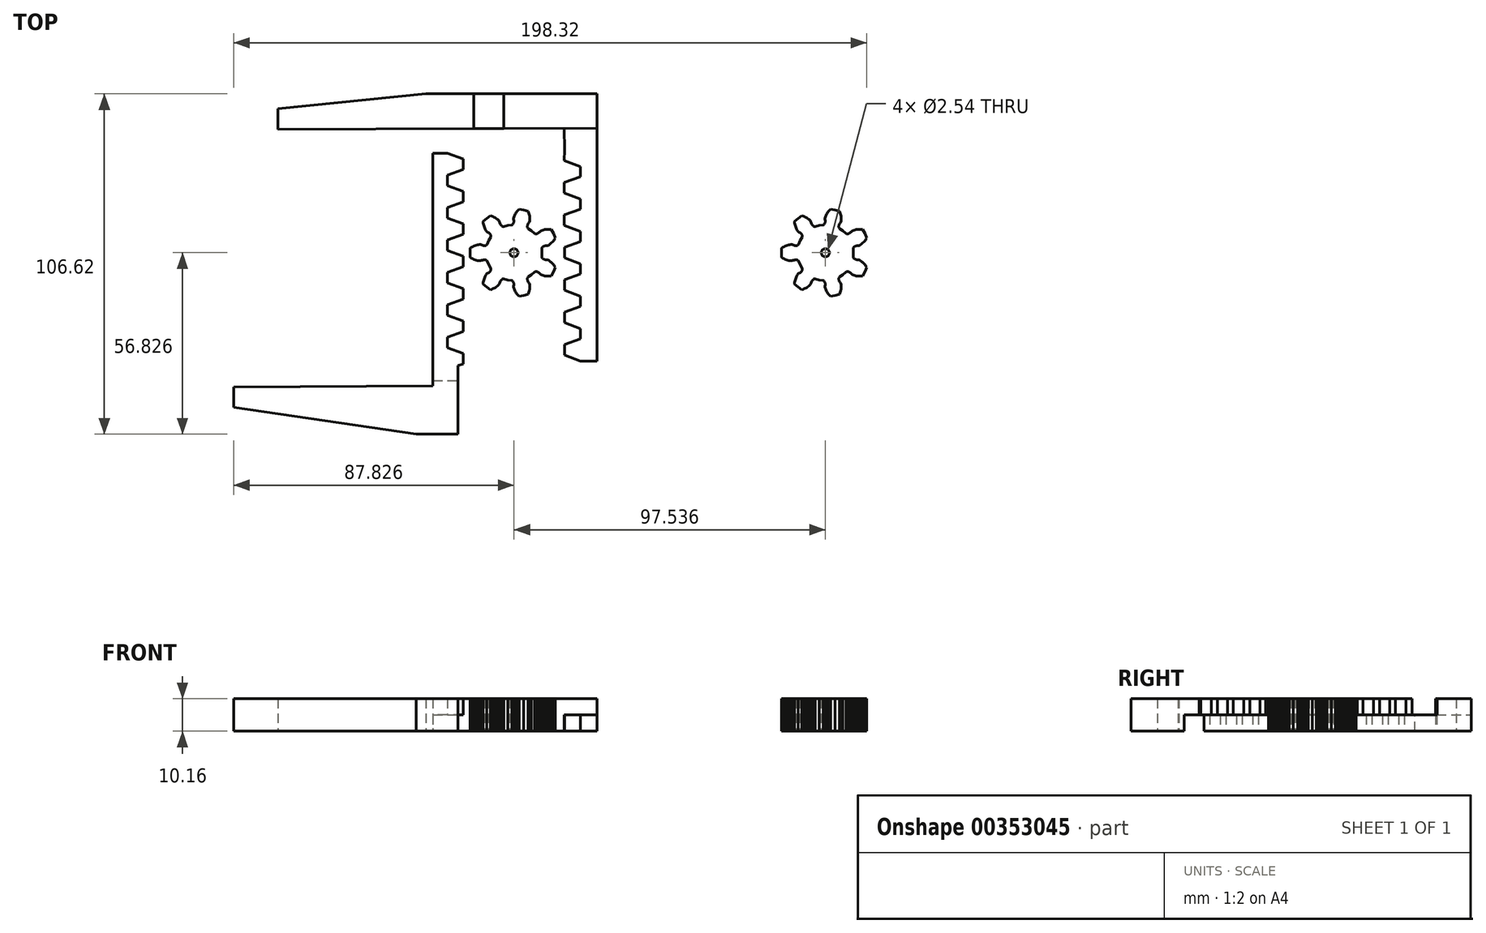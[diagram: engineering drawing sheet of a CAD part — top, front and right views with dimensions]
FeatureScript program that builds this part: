
annotation { "Feature Type Name" : "Feature", "Feature Type Description" : "" }
export const myFeature = defineFeature(function(context is Context, id is Id, definition is map)
    precondition{}
    {
        {
            var Q0;
            Q0=qCreatedBy(makeId("Top.planeOp"),FACE);
            var sketch = newSketch(context, id + "F0", { "sketchPlane" : qUnion([Q0])});
            skLineSegment(sketch, "E0", {"start": v(32.97, 4.76) * mm, "end": v(33, 5.04) * mm});
            skLineSegment(sketch, "E1", {"start": v(33, 5.04) * mm, "end": v(33.07, 5.15) * mm});
            skLineSegment(sketch, "E2", {"start": v(33.07, 5.15) * mm, "end": v(33.14, 5.24) * mm});
            skLineSegment(sketch, "E3", {"start": v(33.14, 5.24) * mm, "end": v(33.2, 5.3) * mm});
            skLineSegment(sketch, "E4", {"start": v(33.2, 5.3) * mm, "end": v(33.28, 5.37) * mm});
            skLineSegment(sketch, "E5", {"start": v(33.28, 5.37) * mm, "end": v(33.36, 5.42) * mm});
            skLineSegment(sketch, "E6", {"start": v(33.36, 5.42) * mm, "end": v(33.5, 5.5) * mm});
            skLineSegment(sketch, "E7", {"start": v(33.5, 5.5) * mm, "end": v(33.66, 5.58) * mm});
            skLineSegment(sketch, "E8", {"start": v(33.66, 5.58) * mm, "end": v(33.82, 5.63) * mm});
            skLineSegment(sketch, "E9", {"start": v(33.82, 5.63) * mm, "end": v(34.14, 5.7) * mm});
            skLineSegment(sketch, "E10", {"start": v(34.14, 5.7) * mm, "end": v(34.47, 5.75) * mm});
            skLineSegment(sketch, "E11", {"start": v(34.47, 5.75) * mm, "end": v(34.8, 5.77) * mm});
            skLineSegment(sketch, "E12", {"start": v(34.8, 5.77) * mm, "end": v(35.12, 5.92) * mm});
            skLineSegment(sketch, "E13", {"start": v(35.12, 5.92) * mm, "end": v(35.41, 6.1) * mm});
            skLineSegment(sketch, "E14", {"start": v(35.41, 6.1) * mm, "end": v(35.7, 6.32) * mm});
            skLineSegment(sketch, "E15", {"start": v(35.7, 6.32) * mm, "end": v(35.98, 6.56) * mm});
            skLineSegment(sketch, "E16", {"start": v(35.98, 6.56) * mm, "end": v(36.25, 6.83) * mm});
            skLineSegment(sketch, "E17", {"start": v(36.25, 6.83) * mm, "end": v(36.52, 7.13) * mm});
            skLineSegment(sketch, "E18", {"start": v(36.52, 7.13) * mm, "end": v(36.77, 7.44) * mm});
            skLineSegment(sketch, "E19", {"start": v(36.77, 7.44) * mm, "end": v(37, 7.78) * mm});
            skLineSegment(sketch, "E20", {"start": v(37, 7.78) * mm, "end": v(37.23, 8.14) * mm});
            skLineSegment(sketch, "E21", {"start": v(37.23, 8.14) * mm, "end": v(36.67, 9.48) * mm});
            skLineSegment(sketch, "E22", {"start": v(36.67, 9.48) * mm, "end": v(35.97, 10.76) * mm});
            skLineSegment(sketch, "E23", {"start": v(35.97, 10.76) * mm, "end": v(35.55, 10.8) * mm});
            skLineSegment(sketch, "E24", {"start": v(35.55, 10.8) * mm, "end": v(35.13, 10.83) * mm});
            skLineSegment(sketch, "E25", {"start": v(35.13, 10.83) * mm, "end": v(34.73, 10.83) * mm});
            skLineSegment(sketch, "E26", {"start": v(34.73, 10.83) * mm, "end": v(34.34, 10.81) * mm});
            skLineSegment(sketch, "E27", {"start": v(34.34, 10.81) * mm, "end": v(33.96, 10.77) * mm});
            skLineSegment(sketch, "E28", {"start": v(33.96, 10.77) * mm, "end": v(33.6, 10.7) * mm});
            skLineSegment(sketch, "E29", {"start": v(33.6, 10.7) * mm, "end": v(33.24, 10.61) * mm});
            skLineSegment(sketch, "E30", {"start": v(33.24, 10.61) * mm, "end": v(32.91, 10.5) * mm});
            skLineSegment(sketch, "E31", {"start": v(32.91, 10.5) * mm, "end": v(32.6, 10.34) * mm});
            skLineSegment(sketch, "E32", {"start": v(32.6, 10.34) * mm, "end": v(32.38, 10.1) * mm});
            skLineSegment(sketch, "E33", {"start": v(32.38, 10.1) * mm, "end": v(32.14, 9.86) * mm});
            skLineSegment(sketch, "E34", {"start": v(32.14, 9.86) * mm, "end": v(31.88, 9.66) * mm});
            skLineSegment(sketch, "E35", {"start": v(31.88, 9.66) * mm, "end": v(31.74, 9.57) * mm});
            skLineSegment(sketch, "E36", {"start": v(31.74, 9.57) * mm, "end": v(31.59, 9.49) * mm});
            skLineSegment(sketch, "E37", {"start": v(31.59, 9.49) * mm, "end": v(31.43, 9.43) * mm});
            skLineSegment(sketch, "E38", {"start": v(31.43, 9.43) * mm, "end": v(31.34, 9.4) * mm});
            skLineSegment(sketch, "E39", {"start": v(31.34, 9.4) * mm, "end": v(31.25, 9.38) * mm});
            skLineSegment(sketch, "E40", {"start": v(31.25, 9.38) * mm, "end": v(31.15, 9.37) * mm});
            skLineSegment(sketch, "E41", {"start": v(31.15, 9.37) * mm, "end": v(31.04, 9.37) * mm});
            skLineSegment(sketch, "E42", {"start": v(31.04, 9.37) * mm, "end": v(30.91, 9.4) * mm});
            skLineSegment(sketch, "E43", {"start": v(30.91, 9.4) * mm, "end": v(30.67, 9.53) * mm});
            skLineSegment(sketch, "E44", {"start": v(30.67, 9.53) * mm, "end": v(29.75, 10.38) * mm});
            skLineSegment(sketch, "E45", {"start": v(29.75, 10.38) * mm, "end": v(28.72, 11.09) * mm});
            skLineSegment(sketch, "E46", {"start": v(28.72, 11.09) * mm, "end": v(28.53, 11.3) * mm});
            skLineSegment(sketch, "E47", {"start": v(28.53, 11.3) * mm, "end": v(28.48, 11.41) * mm});
            skLineSegment(sketch, "E48", {"start": v(28.48, 11.41) * mm, "end": v(28.45, 11.52) * mm});
            skLineSegment(sketch, "E49", {"start": v(28.45, 11.52) * mm, "end": v(28.44, 11.62) * mm});
            skLineSegment(sketch, "E50", {"start": v(28.44, 11.62) * mm, "end": v(28.44, 11.71) * mm});
            skLineSegment(sketch, "E51", {"start": v(28.44, 11.71) * mm, "end": v(28.45, 11.8) * mm});
            skLineSegment(sketch, "E52", {"start": v(28.45, 11.8) * mm, "end": v(28.47, 11.97) * mm});
            skLineSegment(sketch, "E53", {"start": v(28.47, 11.97) * mm, "end": v(28.52, 12.14) * mm});
            skLineSegment(sketch, "E54", {"start": v(28.52, 12.14) * mm, "end": v(28.57, 12.3) * mm});
            skLineSegment(sketch, "E55", {"start": v(28.57, 12.3) * mm, "end": v(28.71, 12.6) * mm});
            skLineSegment(sketch, "E56", {"start": v(28.71, 12.6) * mm, "end": v(28.89, 12.88) * mm});
            skLineSegment(sketch, "E57", {"start": v(28.89, 12.88) * mm, "end": v(29.08, 13.15) * mm});
            skLineSegment(sketch, "E58", {"start": v(29.08, 13.15) * mm, "end": v(29.16, 13.49) * mm});
            skLineSegment(sketch, "E59", {"start": v(29.16, 13.49) * mm, "end": v(29.2, 13.84) * mm});
            skLineSegment(sketch, "E60", {"start": v(29.2, 13.84) * mm, "end": v(29.2, 14.2) * mm});
            skLineSegment(sketch, "E61", {"start": v(29.2, 14.2) * mm, "end": v(29.2, 14.57) * mm});
            skLineSegment(sketch, "E62", {"start": v(29.2, 14.57) * mm, "end": v(29.15, 14.95) * mm});
            skLineSegment(sketch, "E63", {"start": v(29.15, 14.95) * mm, "end": v(29.08, 15.34) * mm});
            skLineSegment(sketch, "E64", {"start": v(29.08, 15.34) * mm, "end": v(29, 15.73) * mm});
            skLineSegment(sketch, "E65", {"start": v(29, 15.73) * mm, "end": v(28.88, 16.13) * mm});
            skLineSegment(sketch, "E66", {"start": v(28.88, 16.13) * mm, "end": v(28.74, 16.53) * mm});
            skLineSegment(sketch, "E67", {"start": v(28.74, 16.53) * mm, "end": v(27.34, 16.93) * mm});
            skLineSegment(sketch, "E68", {"start": v(27.34, 16.93) * mm, "end": v(25.9, 17.18) * mm});
            skLineSegment(sketch, "E69", {"start": v(25.9, 17.18) * mm, "end": v(25.6, 16.87) * mm});
            skLineSegment(sketch, "E70", {"start": v(25.6, 16.87) * mm, "end": v(25.33, 16.57) * mm});
            skLineSegment(sketch, "E71", {"start": v(25.33, 16.57) * mm, "end": v(25.07, 16.25) * mm});
            skLineSegment(sketch, "E72", {"start": v(25.07, 16.25) * mm, "end": v(24.85, 15.93) * mm});
            skLineSegment(sketch, "E73", {"start": v(24.85, 15.93) * mm, "end": v(24.64, 15.6) * mm});
            skLineSegment(sketch, "E74", {"start": v(24.64, 15.6) * mm, "end": v(24.47, 15.28) * mm});
            skLineSegment(sketch, "E75", {"start": v(24.47, 15.28) * mm, "end": v(24.32, 14.95) * mm});
            skLineSegment(sketch, "E76", {"start": v(24.32, 14.95) * mm, "end": v(24.2, 14.62) * mm});
            skLineSegment(sketch, "E77", {"start": v(24.2, 14.62) * mm, "end": v(24.13, 14.28) * mm});
            skLineSegment(sketch, "E78", {"start": v(24.13, 14.28) * mm, "end": v(24.18, 13.95) * mm});
            skLineSegment(sketch, "E79", {"start": v(24.18, 13.95) * mm, "end": v(24.22, 13.62) * mm});
            skLineSegment(sketch, "E80", {"start": v(24.22, 13.62) * mm, "end": v(24.22, 13.3) * mm});
            skLineSegment(sketch, "E81", {"start": v(24.22, 13.3) * mm, "end": v(24.2, 13.12) * mm});
            skLineSegment(sketch, "E82", {"start": v(24.2, 13.12) * mm, "end": v(24.17, 12.96) * mm});
            skLineSegment(sketch, "E83", {"start": v(24.17, 12.96) * mm, "end": v(24.11, 12.8) * mm});
            skLineSegment(sketch, "E84", {"start": v(24.11, 12.8) * mm, "end": v(24.08, 12.7) * mm});
            skLineSegment(sketch, "E85", {"start": v(24.08, 12.7) * mm, "end": v(24.04, 12.62) * mm});
            skLineSegment(sketch, "E86", {"start": v(24.04, 12.62) * mm, "end": v(23.98, 12.54) * mm});
            skLineSegment(sketch, "E87", {"start": v(23.98, 12.54) * mm, "end": v(23.92, 12.45) * mm});
            skLineSegment(sketch, "E88", {"start": v(23.92, 12.45) * mm, "end": v(23.82, 12.37) * mm});
            skLineSegment(sketch, "E89", {"start": v(23.82, 12.37) * mm, "end": v(23.56, 12.27) * mm});
            skLineSegment(sketch, "E90", {"start": v(23.56, 12.27) * mm, "end": v(22.32, 12.07) * mm});
            skLineSegment(sketch, "E91", {"start": v(22.32, 12.07) * mm, "end": v(21.13, 11.7) * mm});
            skLineSegment(sketch, "E92", {"start": v(21.13, 11.7) * mm, "end": v(20.85, 11.69) * mm});
            skLineSegment(sketch, "E93", {"start": v(20.85, 11.69) * mm, "end": v(20.72, 11.72) * mm});
            skLineSegment(sketch, "E94", {"start": v(20.72, 11.72) * mm, "end": v(20.62, 11.77) * mm});
            skLineSegment(sketch, "E95", {"start": v(20.62, 11.77) * mm, "end": v(20.54, 11.83) * mm});
            skLineSegment(sketch, "E96", {"start": v(20.54, 11.83) * mm, "end": v(20.47, 11.88) * mm});
            skLineSegment(sketch, "E97", {"start": v(20.47, 11.88) * mm, "end": v(20.4, 11.94) * mm});
            skLineSegment(sketch, "E98", {"start": v(20.4, 11.94) * mm, "end": v(20.28, 12.07) * mm});
            skLineSegment(sketch, "E99", {"start": v(20.28, 12.07) * mm, "end": v(20.18, 12.2) * mm});
            skLineSegment(sketch, "E100", {"start": v(20.18, 12.2) * mm, "end": v(20.09, 12.35) * mm});
            skLineSegment(sketch, "E101", {"start": v(20.09, 12.35) * mm, "end": v(19.94, 12.65) * mm});
            skLineSegment(sketch, "E102", {"start": v(19.94, 12.65) * mm, "end": v(19.83, 12.96) * mm});
            skLineSegment(sketch, "E103", {"start": v(19.83, 12.96) * mm, "end": v(19.74, 13.28) * mm});
            skLineSegment(sketch, "E104", {"start": v(19.74, 13.28) * mm, "end": v(19.52, 13.55) * mm});
            skLineSegment(sketch, "E105", {"start": v(19.52, 13.55) * mm, "end": v(19.28, 13.8) * mm});
            skLineSegment(sketch, "E106", {"start": v(19.28, 13.8) * mm, "end": v(19, 14.03) * mm});
            skLineSegment(sketch, "E107", {"start": v(19, 14.03) * mm, "end": v(18.7, 14.25) * mm});
            skLineSegment(sketch, "E108", {"start": v(18.7, 14.25) * mm, "end": v(18.38, 14.46) * mm});
            skLineSegment(sketch, "E109", {"start": v(18.38, 14.46) * mm, "end": v(18.03, 14.64) * mm});
            skLineSegment(sketch, "E110", {"start": v(18.03, 14.64) * mm, "end": v(17.67, 14.82) * mm});
            skLineSegment(sketch, "E111", {"start": v(17.67, 14.82) * mm, "end": v(17.29, 14.98) * mm});
            skLineSegment(sketch, "E112", {"start": v(17.29, 14.98) * mm, "end": v(16.89, 15.12) * mm});
            skLineSegment(sketch, "E113", {"start": v(16.89, 15.12) * mm, "end": v(15.7, 14.27) * mm});
            skLineSegment(sketch, "E114", {"start": v(15.7, 14.27) * mm, "end": v(14.6, 13.3) * mm});
            skLineSegment(sketch, "E115", {"start": v(14.6, 13.3) * mm, "end": v(14.66, 12.88) * mm});
            skLineSegment(sketch, "E116", {"start": v(14.66, 12.88) * mm, "end": v(14.73, 12.47) * mm});
            skLineSegment(sketch, "E117", {"start": v(14.73, 12.47) * mm, "end": v(14.82, 12.08) * mm});
            skLineSegment(sketch, "E118", {"start": v(14.82, 12.08) * mm, "end": v(14.92, 11.7) * mm});
            skLineSegment(sketch, "E119", {"start": v(14.92, 11.7) * mm, "end": v(15.05, 11.34) * mm});
            skLineSegment(sketch, "E120", {"start": v(15.05, 11.34) * mm, "end": v(15.2, 11) * mm});
            skLineSegment(sketch, "E121", {"start": v(15.2, 11) * mm, "end": v(15.36, 10.68) * mm});
            skLineSegment(sketch, "E122", {"start": v(15.36, 10.68) * mm, "end": v(15.55, 10.38) * mm});
            skLineSegment(sketch, "E123", {"start": v(15.55, 10.38) * mm, "end": v(15.77, 10.12) * mm});
            skLineSegment(sketch, "E124", {"start": v(15.77, 10.12) * mm, "end": v(16.06, 9.95) * mm});
            skLineSegment(sketch, "E125", {"start": v(16.06, 9.95) * mm, "end": v(16.34, 9.77) * mm});
            skLineSegment(sketch, "E126", {"start": v(16.34, 9.77) * mm, "end": v(16.6, 9.56) * mm});
            skLineSegment(sketch, "E127", {"start": v(16.6, 9.56) * mm, "end": v(16.72, 9.45) * mm});
            skLineSegment(sketch, "E128", {"start": v(16.72, 9.45) * mm, "end": v(16.83, 9.32) * mm});
            skLineSegment(sketch, "E129", {"start": v(16.83, 9.32) * mm, "end": v(16.92, 9.17) * mm});
            skLineSegment(sketch, "E130", {"start": v(16.92, 9.17) * mm, "end": v(16.97, 9.1) * mm});
            skLineSegment(sketch, "E131", {"start": v(16.97, 9.1) * mm, "end": v(17, 9) * mm});
            skLineSegment(sketch, "E132", {"start": v(17, 9) * mm, "end": v(17.04, 8.91) * mm});
            skLineSegment(sketch, "E133", {"start": v(17.04, 8.91) * mm, "end": v(17.06, 8.8) * mm});
            skLineSegment(sketch, "E134", {"start": v(17.06, 8.8) * mm, "end": v(17.07, 8.68) * mm});
            skLineSegment(sketch, "E135", {"start": v(17.07, 8.68) * mm, "end": v(16.99, 8.41) * mm});
            skLineSegment(sketch, "E136", {"start": v(16.99, 8.41) * mm, "end": v(16.37, 7.32) * mm});
            skLineSegment(sketch, "E137", {"start": v(16.37, 7.32) * mm, "end": v(15.9, 6.16) * mm});
            skLineSegment(sketch, "E138", {"start": v(15.9, 6.16) * mm, "end": v(15.75, 5.93) * mm});
            skLineSegment(sketch, "E139", {"start": v(15.75, 5.93) * mm, "end": v(15.64, 5.86) * mm});
            skLineSegment(sketch, "E140", {"start": v(15.64, 5.86) * mm, "end": v(15.54, 5.8) * mm});
            skLineSegment(sketch, "E141", {"start": v(15.54, 5.8) * mm, "end": v(15.45, 5.78) * mm});
            skLineSegment(sketch, "E142", {"start": v(15.45, 5.78) * mm, "end": v(15.36, 5.75) * mm});
            skLineSegment(sketch, "E143", {"start": v(15.36, 5.75) * mm, "end": v(15.27, 5.74) * mm});
            skLineSegment(sketch, "E144", {"start": v(15.27, 5.74) * mm, "end": v(15.1, 5.72) * mm});
            skLineSegment(sketch, "E145", {"start": v(15.1, 5.72) * mm, "end": v(14.93, 5.73) * mm});
            skLineSegment(sketch, "E146", {"start": v(14.93, 5.73) * mm, "end": v(14.76, 5.75) * mm});
            skLineSegment(sketch, "E147", {"start": v(14.76, 5.75) * mm, "end": v(14.44, 5.82) * mm});
            skLineSegment(sketch, "E148", {"start": v(14.44, 5.82) * mm, "end": v(14.12, 5.93) * mm});
            skLineSegment(sketch, "E149", {"start": v(14.12, 5.93) * mm, "end": v(13.81, 6.05) * mm});
            skLineSegment(sketch, "E150", {"start": v(13.81, 6.05) * mm, "end": v(13.47, 6.06) * mm});
            skLineSegment(sketch, "E151", {"start": v(13.47, 6.06) * mm, "end": v(13.12, 6.02) * mm});
            skLineSegment(sketch, "E152", {"start": v(13.12, 6.02) * mm, "end": v(12.76, 5.95) * mm});
            skLineSegment(sketch, "E153", {"start": v(12.76, 5.95) * mm, "end": v(12.4, 5.85) * mm});
            skLineSegment(sketch, "E154", {"start": v(12.4, 5.85) * mm, "end": v(12.04, 5.72) * mm});
            skLineSegment(sketch, "E155", {"start": v(12.04, 5.72) * mm, "end": v(11.68, 5.57) * mm});
            skLineSegment(sketch, "E156", {"start": v(11.68, 5.57) * mm, "end": v(11.32, 5.4) * mm});
            skLineSegment(sketch, "E157", {"start": v(11.32, 5.4) * mm, "end": v(10.96, 5.2) * mm});
            skLineSegment(sketch, "E158", {"start": v(10.96, 5.2) * mm, "end": v(10.6, 4.97) * mm});
            skLineSegment(sketch, "E159", {"start": v(10.6, 4.97) * mm, "end": v(10.52, 3.52) * mm});
            skLineSegment(sketch, "E160", {"start": v(10.52, 3.52) * mm, "end": v(10.6, 2.06) * mm});
            skLineSegment(sketch, "E161", {"start": v(10.6, 2.06) * mm, "end": v(10.96, 1.84) * mm});
            skLineSegment(sketch, "E162", {"start": v(10.96, 1.84) * mm, "end": v(11.32, 1.64) * mm});
            skLineSegment(sketch, "E163", {"start": v(11.32, 1.64) * mm, "end": v(11.68, 1.46) * mm});
            skLineSegment(sketch, "E164", {"start": v(11.68, 1.46) * mm, "end": v(12.04, 1.3) * mm});
            skLineSegment(sketch, "E165", {"start": v(12.04, 1.3) * mm, "end": v(12.4, 1.18) * mm});
            skLineSegment(sketch, "E166", {"start": v(12.4, 1.18) * mm, "end": v(12.76, 1.08) * mm});
            skLineSegment(sketch, "E167", {"start": v(12.76, 1.08) * mm, "end": v(13.12, 1.01) * mm});
            skLineSegment(sketch, "E168", {"start": v(13.12, 1.01) * mm, "end": v(13.47, 0.98) * mm});
            skLineSegment(sketch, "E169", {"start": v(13.47, 0.98) * mm, "end": v(13.81, 0.98) * mm});
            skLineSegment(sketch, "E170", {"start": v(13.81, 0.98) * mm, "end": v(14.12, 1.1) * mm});
            skLineSegment(sketch, "E171", {"start": v(14.12, 1.1) * mm, "end": v(14.44, 1.21) * mm});
            skLineSegment(sketch, "E172", {"start": v(14.44, 1.21) * mm, "end": v(14.76, 1.28) * mm});
            skLineSegment(sketch, "E173", {"start": v(14.76, 1.28) * mm, "end": v(14.93, 1.3) * mm});
            skLineSegment(sketch, "E174", {"start": v(14.93, 1.3) * mm, "end": v(15.1, 1.3) * mm});
            skLineSegment(sketch, "E175", {"start": v(15.1, 1.3) * mm, "end": v(15.27, 1.3) * mm});
            skLineSegment(sketch, "E176", {"start": v(15.27, 1.3) * mm, "end": v(15.36, 1.28) * mm});
            skLineSegment(sketch, "E177", {"start": v(15.36, 1.28) * mm, "end": v(15.45, 1.26) * mm});
            skLineSegment(sketch, "E178", {"start": v(15.45, 1.26) * mm, "end": v(15.54, 1.22) * mm});
            skLineSegment(sketch, "E179", {"start": v(15.54, 1.22) * mm, "end": v(15.64, 1.18) * mm});
            skLineSegment(sketch, "E180", {"start": v(15.64, 1.18) * mm, "end": v(15.75, 1.1) * mm});
            skLineSegment(sketch, "E181", {"start": v(15.75, 1.1) * mm, "end": v(15.9, 0.87) * mm});
            skLineSegment(sketch, "E182", {"start": v(15.9, 0.87) * mm, "end": v(16.37, -0.3) * mm});
            skLineSegment(sketch, "E183", {"start": v(16.37, -0.3) * mm, "end": v(16.99, -1.38) * mm});
            skLineSegment(sketch, "E184", {"start": v(16.99, -1.38) * mm, "end": v(17.07, -1.64) * mm});
            skLineSegment(sketch, "E185", {"start": v(17.07, -1.64) * mm, "end": v(17.06, -1.78) * mm});
            skLineSegment(sketch, "E186", {"start": v(17.06, -1.78) * mm, "end": v(17.04, -1.88) * mm});
            skLineSegment(sketch, "E187", {"start": v(17.04, -1.88) * mm, "end": v(17, -1.98) * mm});
            skLineSegment(sketch, "E188", {"start": v(17, -1.98) * mm, "end": v(16.97, -2.06) * mm});
            skLineSegment(sketch, "E189", {"start": v(16.97, -2.06) * mm, "end": v(16.92, -2.14) * mm});
            skLineSegment(sketch, "E190", {"start": v(16.92, -2.14) * mm, "end": v(16.83, -2.28) * mm});
            skLineSegment(sketch, "E191", {"start": v(16.83, -2.28) * mm, "end": v(16.72, -2.41) * mm});
            skLineSegment(sketch, "E192", {"start": v(16.72, -2.41) * mm, "end": v(16.6, -2.53) * mm});
            skLineSegment(sketch, "E193", {"start": v(16.6, -2.53) * mm, "end": v(16.34, -2.74) * mm});
            skLineSegment(sketch, "E194", {"start": v(16.34, -2.74) * mm, "end": v(16.06, -2.92) * mm});
            skLineSegment(sketch, "E195", {"start": v(16.06, -2.92) * mm, "end": v(15.77, -3.08) * mm});
            skLineSegment(sketch, "E196", {"start": v(15.77, -3.08) * mm, "end": v(15.55, -3.35) * mm});
            skLineSegment(sketch, "E197", {"start": v(15.55, -3.35) * mm, "end": v(15.36, -3.65) * mm});
            skLineSegment(sketch, "E198", {"start": v(15.36, -3.65) * mm, "end": v(15.2, -3.97) * mm});
            skLineSegment(sketch, "E199", {"start": v(15.2, -3.97) * mm, "end": v(15.05, -4.31) * mm});
            skLineSegment(sketch, "E200", {"start": v(15.05, -4.31) * mm, "end": v(14.92, -4.67) * mm});
            skLineSegment(sketch, "E201", {"start": v(14.92, -4.67) * mm, "end": v(14.82, -5.05) * mm});
            skLineSegment(sketch, "E202", {"start": v(14.82, -5.05) * mm, "end": v(14.73, -5.44) * mm});
            skLineSegment(sketch, "E203", {"start": v(14.73, -5.44) * mm, "end": v(14.66, -5.85) * mm});
            skLineSegment(sketch, "E204", {"start": v(14.66, -5.85) * mm, "end": v(14.6, -6.27) * mm});
            skLineSegment(sketch, "E205", {"start": v(14.6, -6.27) * mm, "end": v(15.7, -7.24) * mm});
            skLineSegment(sketch, "E206", {"start": v(15.7, -7.24) * mm, "end": v(16.89, -8.09) * mm});
            skLineSegment(sketch, "E207", {"start": v(16.89, -8.09) * mm, "end": v(17.29, -7.94) * mm});
            skLineSegment(sketch, "E208", {"start": v(17.29, -7.94) * mm, "end": v(17.67, -7.79) * mm});
            skLineSegment(sketch, "E209", {"start": v(17.67, -7.79) * mm, "end": v(18.03, -7.61) * mm});
            skLineSegment(sketch, "E210", {"start": v(18.03, -7.61) * mm, "end": v(18.38, -7.42) * mm});
            skLineSegment(sketch, "E211", {"start": v(18.38, -7.42) * mm, "end": v(18.7, -7.22) * mm});
            skLineSegment(sketch, "E212", {"start": v(18.7, -7.22) * mm, "end": v(19, -7) * mm});
            skLineSegment(sketch, "E213", {"start": v(19, -7) * mm, "end": v(19.28, -6.77) * mm});
            skLineSegment(sketch, "E214", {"start": v(19.28, -6.77) * mm, "end": v(19.52, -6.52) * mm});
            skLineSegment(sketch, "E215", {"start": v(19.52, -6.52) * mm, "end": v(19.74, -6.25) * mm});
            skLineSegment(sketch, "E216", {"start": v(19.74, -6.25) * mm, "end": v(19.83, -5.93) * mm});
            skLineSegment(sketch, "E217", {"start": v(19.83, -5.93) * mm, "end": v(19.94, -5.61) * mm});
            skLineSegment(sketch, "E218", {"start": v(19.94, -5.61) * mm, "end": v(20.09, -5.32) * mm});
            skLineSegment(sketch, "E219", {"start": v(20.09, -5.32) * mm, "end": v(20.18, -5.18) * mm});
            skLineSegment(sketch, "E220", {"start": v(20.18, -5.18) * mm, "end": v(20.28, -5.04) * mm});
            skLineSegment(sketch, "E221", {"start": v(20.28, -5.04) * mm, "end": v(20.4, -4.91) * mm});
            skLineSegment(sketch, "E222", {"start": v(20.4, -4.91) * mm, "end": v(20.47, -4.85) * mm});
            skLineSegment(sketch, "E223", {"start": v(20.47, -4.85) * mm, "end": v(20.54, -4.8) * mm});
            skLineSegment(sketch, "E224", {"start": v(20.54, -4.8) * mm, "end": v(20.62, -4.74) * mm});
            skLineSegment(sketch, "E225", {"start": v(20.62, -4.74) * mm, "end": v(20.72, -4.7) * mm});
            skLineSegment(sketch, "E226", {"start": v(20.72, -4.7) * mm, "end": v(20.85, -4.66) * mm});
            skLineSegment(sketch, "E227", {"start": v(20.85, -4.66) * mm, "end": v(21.13, -4.68) * mm});
            skLineSegment(sketch, "E228", {"start": v(21.13, -4.68) * mm, "end": v(22.32, -5.04) * mm});
            skLineSegment(sketch, "E229", {"start": v(22.32, -5.04) * mm, "end": v(23.56, -5.23) * mm});
            skLineSegment(sketch, "E230", {"start": v(23.56, -5.23) * mm, "end": v(23.82, -5.33) * mm});
            skLineSegment(sketch, "E231", {"start": v(23.82, -5.33) * mm, "end": v(23.92, -5.42) * mm});
            skLineSegment(sketch, "E232", {"start": v(23.92, -5.42) * mm, "end": v(23.98, -5.5) * mm});
            skLineSegment(sketch, "E233", {"start": v(23.98, -5.5) * mm, "end": v(24.04, -5.6) * mm});
            skLineSegment(sketch, "E234", {"start": v(24.04, -5.6) * mm, "end": v(24.08, -5.68) * mm});
            skLineSegment(sketch, "E235", {"start": v(24.08, -5.68) * mm, "end": v(24.11, -5.76) * mm});
            skLineSegment(sketch, "E236", {"start": v(24.11, -5.76) * mm, "end": v(24.17, -5.93) * mm});
            skLineSegment(sketch, "E237", {"start": v(24.17, -5.93) * mm, "end": v(24.2, -6.1) * mm});
            skLineSegment(sketch, "E238", {"start": v(24.2, -6.1) * mm, "end": v(24.22, -6.26) * mm});
            skLineSegment(sketch, "E239", {"start": v(24.22, -6.26) * mm, "end": v(24.22, -6.6) * mm});
            skLineSegment(sketch, "E240", {"start": v(24.22, -6.6) * mm, "end": v(24.18, -6.92) * mm});
            skLineSegment(sketch, "E241", {"start": v(24.18, -6.92) * mm, "end": v(24.13, -7.25) * mm});
            skLineSegment(sketch, "E242", {"start": v(24.13, -7.25) * mm, "end": v(24.2, -7.59) * mm});
            skLineSegment(sketch, "E243", {"start": v(24.2, -7.59) * mm, "end": v(24.32, -7.92) * mm});
            skLineSegment(sketch, "E244", {"start": v(24.32, -7.92) * mm, "end": v(24.47, -8.25) * mm});
            skLineSegment(sketch, "E245", {"start": v(24.47, -8.25) * mm, "end": v(24.64, -8.58) * mm});
            skLineSegment(sketch, "E246", {"start": v(24.64, -8.58) * mm, "end": v(24.85, -8.9) * mm});
            skLineSegment(sketch, "E247", {"start": v(24.85, -8.9) * mm, "end": v(25.07, -9.22) * mm});
            skLineSegment(sketch, "E248", {"start": v(25.07, -9.22) * mm, "end": v(25.33, -9.53) * mm});
            skLineSegment(sketch, "E249", {"start": v(25.33, -9.53) * mm, "end": v(25.6, -9.84) * mm});
            skLineSegment(sketch, "E250", {"start": v(25.6, -9.84) * mm, "end": v(25.9, -10.14) * mm});
            skLineSegment(sketch, "E251", {"start": v(25.9, -10.14) * mm, "end": v(27.34, -9.9) * mm});
            skLineSegment(sketch, "E252", {"start": v(27.34, -9.9) * mm, "end": v(28.74, -9.5) * mm});
            skLineSegment(sketch, "E253", {"start": v(28.74, -9.5) * mm, "end": v(28.88, -9.1) * mm});
            skLineSegment(sketch, "E254", {"start": v(28.88, -9.1) * mm, "end": v(29, -8.7) * mm});
            skLineSegment(sketch, "E255", {"start": v(29, -8.7) * mm, "end": v(29.08, -8.3) * mm});
            skLineSegment(sketch, "E256", {"start": v(29.08, -8.3) * mm, "end": v(29.15, -7.92) * mm});
            skLineSegment(sketch, "E257", {"start": v(29.15, -7.92) * mm, "end": v(29.2, -7.54) * mm});
            skLineSegment(sketch, "E258", {"start": v(29.2, -7.54) * mm, "end": v(29.2, -7.17) * mm});
            skLineSegment(sketch, "E259", {"start": v(29.2, -7.17) * mm, "end": v(29.2, -6.8) * mm});
            skLineSegment(sketch, "E260", {"start": v(29.2, -6.8) * mm, "end": v(29.16, -6.46) * mm});
            skLineSegment(sketch, "E261", {"start": v(29.16, -6.46) * mm, "end": v(29.08, -6.12) * mm});
            skLineSegment(sketch, "E262", {"start": v(29.08, -6.12) * mm, "end": v(28.89, -5.85) * mm});
            skLineSegment(sketch, "E263", {"start": v(28.89, -5.85) * mm, "end": v(28.71, -5.56) * mm});
            skLineSegment(sketch, "E264", {"start": v(28.71, -5.56) * mm, "end": v(28.57, -5.26) * mm});
            skLineSegment(sketch, "E265", {"start": v(28.57, -5.26) * mm, "end": v(28.52, -5.1) * mm});
            skLineSegment(sketch, "E266", {"start": v(28.52, -5.1) * mm, "end": v(28.47, -4.94) * mm});
            skLineSegment(sketch, "E267", {"start": v(28.47, -4.94) * mm, "end": v(28.45, -4.77) * mm});
            skLineSegment(sketch, "E268", {"start": v(28.45, -4.77) * mm, "end": v(28.44, -4.68) * mm});
            skLineSegment(sketch, "E269", {"start": v(28.44, -4.68) * mm, "end": v(28.44, -4.59) * mm});
            skLineSegment(sketch, "E270", {"start": v(28.44, -4.59) * mm, "end": v(28.45, -4.49) * mm});
            skLineSegment(sketch, "E271", {"start": v(28.45, -4.49) * mm, "end": v(28.48, -4.38) * mm});
            skLineSegment(sketch, "E272", {"start": v(28.48, -4.38) * mm, "end": v(28.53, -4.26) * mm});
            skLineSegment(sketch, "E273", {"start": v(28.53, -4.26) * mm, "end": v(28.72, -4.06) * mm});
            skLineSegment(sketch, "E274", {"start": v(28.72, -4.06) * mm, "end": v(29.75, -3.35) * mm});
            skLineSegment(sketch, "E275", {"start": v(29.75, -3.35) * mm, "end": v(30.67, -2.5) * mm});
            skLineSegment(sketch, "E276", {"start": v(30.67, -2.5) * mm, "end": v(30.91, -2.36) * mm});
            skLineSegment(sketch, "E277", {"start": v(30.91, -2.36) * mm, "end": v(31.04, -2.34) * mm});
            skLineSegment(sketch, "E278", {"start": v(31.04, -2.34) * mm, "end": v(31.15, -2.34) * mm});
            skLineSegment(sketch, "E279", {"start": v(31.15, -2.34) * mm, "end": v(31.25, -2.35) * mm});
            skLineSegment(sketch, "E280", {"start": v(31.25, -2.35) * mm, "end": v(31.34, -2.37) * mm});
            skLineSegment(sketch, "E281", {"start": v(31.34, -2.37) * mm, "end": v(31.43, -2.4) * mm});
            skLineSegment(sketch, "E282", {"start": v(31.43, -2.4) * mm, "end": v(31.59, -2.46) * mm});
            skLineSegment(sketch, "E283", {"start": v(31.59, -2.46) * mm, "end": v(31.74, -2.54) * mm});
            skLineSegment(sketch, "E284", {"start": v(31.74, -2.54) * mm, "end": v(31.88, -2.63) * mm});
            skLineSegment(sketch, "E285", {"start": v(31.88, -2.63) * mm, "end": v(32.14, -2.83) * mm});
            skLineSegment(sketch, "E286", {"start": v(32.14, -2.83) * mm, "end": v(32.38, -3.07) * mm});
            skLineSegment(sketch, "E287", {"start": v(32.38, -3.07) * mm, "end": v(32.6, -3.31) * mm});
            skLineSegment(sketch, "E288", {"start": v(32.6, -3.31) * mm, "end": v(32.91, -3.46) * mm});
            skLineSegment(sketch, "E289", {"start": v(32.91, -3.46) * mm, "end": v(33.24, -3.58) * mm});
            skLineSegment(sketch, "E290", {"start": v(33.24, -3.58) * mm, "end": v(33.6, -3.67) * mm});
            skLineSegment(sketch, "E291", {"start": v(33.6, -3.67) * mm, "end": v(33.96, -3.74) * mm});
            skLineSegment(sketch, "E292", {"start": v(33.96, -3.74) * mm, "end": v(34.34, -3.78) * mm});
            skLineSegment(sketch, "E293", {"start": v(34.34, -3.78) * mm, "end": v(34.73, -3.8) * mm});
            skLineSegment(sketch, "E294", {"start": v(34.73, -3.8) * mm, "end": v(35.13, -3.8) * mm});
            skLineSegment(sketch, "E295", {"start": v(35.13, -3.8) * mm, "end": v(35.55, -3.78) * mm});
            skLineSegment(sketch, "E296", {"start": v(35.55, -3.78) * mm, "end": v(35.97, -3.73) * mm});
            skLineSegment(sketch, "E297", {"start": v(35.97, -3.73) * mm, "end": v(36.67, -2.45) * mm});
            skLineSegment(sketch, "E298", {"start": v(36.67, -2.45) * mm, "end": v(37.23, -1.1) * mm});
            skLineSegment(sketch, "E299", {"start": v(37.23, -1.1) * mm, "end": v(37, -0.75) * mm});
            skLineSegment(sketch, "E300", {"start": v(37, -0.75) * mm, "end": v(36.77, -0.41) * mm});
            skLineSegment(sketch, "E301", {"start": v(36.77, -0.41) * mm, "end": v(36.52, -0.1) * mm});
            skLineSegment(sketch, "E302", {"start": v(36.52, -0.1) * mm, "end": v(36.25, 0.2) * mm});
            skLineSegment(sketch, "E303", {"start": v(36.25, 0.2) * mm, "end": v(35.98, 0.47) * mm});
            skLineSegment(sketch, "E304", {"start": v(35.98, 0.47) * mm, "end": v(35.7, 0.71) * mm});
            skLineSegment(sketch, "E305", {"start": v(35.7, 0.71) * mm, "end": v(35.41, 0.93) * mm});
            skLineSegment(sketch, "E306", {"start": v(35.41, 0.93) * mm, "end": v(35.12, 1.12) * mm});
            skLineSegment(sketch, "E307", {"start": v(35.12, 1.12) * mm, "end": v(34.8, 1.26) * mm});
            skLineSegment(sketch, "E308", {"start": v(34.8, 1.26) * mm, "end": v(34.47, 1.28) * mm});
            skLineSegment(sketch, "E309", {"start": v(34.47, 1.28) * mm, "end": v(34.14, 1.32) * mm});
            skLineSegment(sketch, "E310", {"start": v(34.14, 1.32) * mm, "end": v(33.82, 1.4) * mm});
            skLineSegment(sketch, "E311", {"start": v(33.82, 1.4) * mm, "end": v(33.66, 1.45) * mm});
            skLineSegment(sketch, "E312", {"start": v(33.66, 1.45) * mm, "end": v(33.5, 1.52) * mm});
            skLineSegment(sketch, "E313", {"start": v(33.5, 1.52) * mm, "end": v(33.36, 1.6) * mm});
            skLineSegment(sketch, "E314", {"start": v(33.36, 1.6) * mm, "end": v(33.28, 1.66) * mm});
            skLineSegment(sketch, "E315", {"start": v(33.28, 1.66) * mm, "end": v(33.2, 1.72) * mm});
            skLineSegment(sketch, "E316", {"start": v(33.2, 1.72) * mm, "end": v(33.14, 1.8) * mm});
            skLineSegment(sketch, "E317", {"start": v(33.14, 1.8) * mm, "end": v(33.07, 1.88) * mm});
            skLineSegment(sketch, "E318", {"start": v(33.07, 1.88) * mm, "end": v(33, 2) * mm});
            skLineSegment(sketch, "E319", {"start": v(33, 2) * mm, "end": v(32.97, 2.27) * mm});
            skLineSegment(sketch, "E320", {"start": v(32.97, 2.27) * mm, "end": v(33.06, 3.52) * mm});
            skLineSegment(sketch, "E321", {"start": v(33.06, 3.52) * mm, "end": v(32.97, 4.76) * mm});
            skLineSegment(sketch, "E322", {"start": v(40.08, 35.67) * mm, "end": v(40.05, 32.36) * mm});
            skLineSegment(sketch, "E323", {"start": v(40.05, 32.36) * mm, "end": v(45.06, 30.55) * mm});
            skLineSegment(sketch, "E324", {"start": v(45.06, -20.25) * mm, "end": v(45.06, -23.48) * mm});
            skLineSegment(sketch, "E325", {"start": v(45.06, -23.48) * mm, "end": v(40.08, -25.3) * mm});
            skLineSegment(sketch, "E326", {"start": v(40.08, -25.3) * mm, "end": v(40.08, -28.6) * mm});
            skLineSegment(sketch, "E327", {"start": v(40.08, -28.6) * mm, "end": v(45.06, -30.4) * mm});
            skLineSegment(sketch, "E328", {"start": v(45.06, -30.4) * mm, "end": v(50.28, -30.41) * mm});
            skLineSegment(sketch, "E329", {"start": v(50.28, -30.41) * mm, "end": v(50.28, 53.3) * mm});
            skLineSegment(sketch, "E330", {"start": v(45.03, 30.55) * mm, "end": v(45.03, 27.32) * mm});
            skLineSegment(sketch, "E331", {"start": v(45.03, 27.32) * mm, "end": v(40.05, 25.5) * mm});
            skLineSegment(sketch, "E332", {"start": v(40.05, 25.5) * mm, "end": v(40.06, 22.2) * mm});
            skLineSegment(sketch, "E333", {"start": v(40.06, 22.2) * mm, "end": v(45.03, 20.4) * mm});
            skLineSegment(sketch, "E334", {"start": v(45.03, 20.4) * mm, "end": v(45.04, 17.16) * mm});
            skLineSegment(sketch, "E335", {"start": v(45.04, 17.16) * mm, "end": v(40.06, 15.35) * mm});
            skLineSegment(sketch, "E336", {"start": v(40.06, 15.35) * mm, "end": v(40.06, 12.04) * mm});
            skLineSegment(sketch, "E337", {"start": v(40.06, 12.04) * mm, "end": v(45.04, 10.23) * mm});
            skLineSegment(sketch, "E338", {"start": v(45.04, 10.23) * mm, "end": v(45.04, 7) * mm});
            skLineSegment(sketch, "E339", {"start": v(45.04, 7) * mm, "end": v(40.07, 5.19) * mm});
            skLineSegment(sketch, "E340", {"start": v(40.07, 5.19) * mm, "end": v(40.07, 1.88) * mm});
            skLineSegment(sketch, "E341", {"start": v(40.07, 1.88) * mm, "end": v(45.05, 0.07) * mm});
            skLineSegment(sketch, "E342", {"start": v(45.05, 0.07) * mm, "end": v(45.05, -3.16) * mm});
            skLineSegment(sketch, "E343", {"start": v(45.05, -3.16) * mm, "end": v(40.07, -4.97) * mm});
            skLineSegment(sketch, "E344", {"start": v(40.07, -4.97) * mm, "end": v(40.07, -8.28) * mm});
            skLineSegment(sketch, "E345", {"start": v(40.07, -8.28) * mm, "end": v(45.05, -10.09) * mm});
            skLineSegment(sketch, "E346", {"start": v(45.05, -10.09) * mm, "end": v(45.05, -13.32) * mm});
            skLineSegment(sketch, "E347", {"start": v(45.05, -13.32) * mm, "end": v(40.08, -15.13) * mm});
            skLineSegment(sketch, "E348", {"start": v(40.08, -15.13) * mm, "end": v(40.08, -18.44) * mm});
            skLineSegment(sketch, "E349", {"start": v(40.08, -18.44) * mm, "end": v(45.06, -20.25) * mm});
            skLineSegment(sketch, "E350", {"start": v(3.36, -26.23) * mm, "end": v(3.36, -23) * mm});
            skLineSegment(sketch, "E351", {"start": v(3.36, -23) * mm, "end": v(8.34, -21.19) * mm});
            skLineSegment(sketch, "E352", {"start": v(8.34, -21.19) * mm, "end": v(8.34, -17.88) * mm});
            skLineSegment(sketch, "E353", {"start": v(8.34, -17.88) * mm, "end": v(3.36, -16.07) * mm});
            skLineSegment(sketch, "E354", {"start": v(3.36, -16.07) * mm, "end": v(3.36, -12.84) * mm});
            skLineSegment(sketch, "E355", {"start": v(3.36, -12.84) * mm, "end": v(8.34, -11.03) * mm});
            skLineSegment(sketch, "E356", {"start": v(8.34, -11.03) * mm, "end": v(8.34, -7.72) * mm});
            skLineSegment(sketch, "E357", {"start": v(8.34, -7.72) * mm, "end": v(3.36, -5.9) * mm});
            skLineSegment(sketch, "E358", {"start": v(3.36, -5.9) * mm, "end": v(3.36, -2.68) * mm});
            skLineSegment(sketch, "E359", {"start": v(3.36, -2.68) * mm, "end": v(8.34, -0.87) * mm});
            skLineSegment(sketch, "E360", {"start": v(8.34, -0.87) * mm, "end": v(8.34, 2.44) * mm});
            skLineSegment(sketch, "E361", {"start": v(8.34, 2.44) * mm, "end": v(3.36, 4.25) * mm});
            skLineSegment(sketch, "E362", {"start": v(3.36, 4.25) * mm, "end": v(3.36, 7.48) * mm});
            skLineSegment(sketch, "E363", {"start": v(3.36, 7.48) * mm, "end": v(8.34, 9.3) * mm});
            skLineSegment(sketch, "E364", {"start": v(8.34, 9.3) * mm, "end": v(8.34, 12.6) * mm});
            skLineSegment(sketch, "E365", {"start": v(8.34, 12.6) * mm, "end": v(3.36, 14.41) * mm});
            skLineSegment(sketch, "E366", {"start": v(3.36, 14.41) * mm, "end": v(3.36, 17.64) * mm});
            skLineSegment(sketch, "E367", {"start": v(3.36, 17.64) * mm, "end": v(8.34, 19.45) * mm});
            skLineSegment(sketch, "E368", {"start": v(8.34, 19.45) * mm, "end": v(8.34, 22.76) * mm});
            skLineSegment(sketch, "E369", {"start": v(8.34, 22.76) * mm, "end": v(3.36, 24.57) * mm});
            skLineSegment(sketch, "E370", {"start": v(6.78, -31.92) * mm, "end": v(8.34, -31.35) * mm});
            skLineSegment(sketch, "E371", {"start": v(8.34, -31.35) * mm, "end": v(8.34, -28.04) * mm});
            skLineSegment(sketch, "E372", {"start": v(8.34, -28.04) * mm, "end": v(3.36, -26.23) * mm});
            skLineSegment(sketch, "E373", {"start": v(3.36, 24.57) * mm, "end": v(3.36, 27.8) * mm});
            skLineSegment(sketch, "E374", {"start": v(3.36, 27.8) * mm, "end": v(8.34, 29.61) * mm});
            skLineSegment(sketch, "E375", {"start": v(8.34, 29.61) * mm, "end": v(8.34, 32.92) * mm});
            skLineSegment(sketch, "E376", {"start": v(8.34, 32.92) * mm, "end": v(3.36, 34.73) * mm});
            skLineSegment(sketch, "E377", {"start": v(3.36, 34.73) * mm, "end": v(-1.12, 34.73) * mm});
            skLineSegment(sketch, "E378", {"start": v(-1.12, 34.73) * mm, "end": v(-1.12, -38.22) * mm});
            skLineSegment(sketch, "E379", {"start": v(50.28, 53.3) * mm, "end": v(-3.36, 53.3) * mm});
            skLineSegment(sketch, "E380", {"start": v(-3.36, 53.3) * mm, "end": v(-49.62, 48.6) * mm});
            skLineSegment(sketch, "E381", {"start": v(-49.62, 48.6) * mm, "end": v(-49.62, 42.17) * mm});
            skLineSegment(sketch, "E382", {"start": v(-49.62, 42.17) * mm, "end": v(40.05, 42.54) * mm});
            skLineSegment(sketch, "E383", {"start": v(-1.12, -38.22) * mm, "end": v(-63.55, -38.56) * mm});
            skLineSegment(sketch, "E384", {"start": v(-63.55, -38.56) * mm, "end": v(-63.55, -44.99) * mm});
            skLineSegment(sketch, "E385", {"start": v(-63.55, -44.99) * mm, "end": v(-6.33, -53.3) * mm});
            skLineSegment(sketch, "E386", {"start": v(-6.33, -53.3) * mm, "end": v(6.78, -53.3) * mm});
            skLineSegment(sketch, "E387", {"start": v(6.78, -53.3) * mm, "end": v(6.78, -31.92) * mm});
            skLineSegment(sketch, "E388", {"start": v(40.08, 35.67) * mm, "end": v(40.05, 42.54) * mm});
            skLineSegment(sketch, "E389", {"start": v(8.34, -28.04) * mm, "end": v(-1.12, -28.04) * mm, "construction": true});
            skLineSegment(sketch, "E390.0", {"start": v(11.49, 42.42) * mm, "end": v(11.51, 53.3) * mm});
            skLineSegment(sketch, "E391.0", {"start": v(21.01, 42.46) * mm, "end": v(21.04, 53.3) * mm});
            skLineSegment(sketch, "E392", {"start": v(21.01, 42.46) * mm, "end": v(40.05, 42.54) * mm});
            skLineSegment(sketch, "E393", {"start": v(50.28, 53.3) * mm, "end": v(21.04, 53.3) * mm});
            skLineSegment(sketch, "E394", {"start": v(21.04, 53.3) * mm, "end": v(21.01, 42.46) * mm});
            skLineSegment(sketch, "E395", {"start": v(40.05, 42.54) * mm, "end": v(40.05, 32.36) * mm});
            skLineSegment(sketch, "E396", {"start": v(45.06, 30.55) * mm, "end": v(45.03, 27.32) * mm});
            skLineSegment(sketch, "E397", {"start": v(-1.12, -36.62) * mm, "end": v(6.78, -36.62) * mm});
            skLineSegment(sketch, "E398", {"start": v(40.07, 5.19) * mm, "end": v(50.28, 5.19) * mm, "construction": true});
            skLineSegment(sketch, "E399", {"start": v(22.32, -5.04) * mm, "end": v(27.34, 16.93) * mm});
            skLineSegment(sketch, "E400", {"start": v(29.75, -3.35) * mm, "end": v(15.7, 14.27) * mm});
            skLineSegment(sketch, "E401", {"start": v(10.52, 3.52) * mm, "end": v(33.06, 3.52) * mm});
            skCircle(sketch, "E402", {"center": v(24.28, 3.52) * mm, "radius": 1.27 * mm});
            skSolve(sketch);
        }
        {
            var Q0;
            Q0=makeQuery(id+"F0.imprint","IMPRINT",FACE,{"disambiguationData":[TD([[makeQuery(id+"F0.imprint","IMPRINT",EDGE,{"derivedFrom":sQuery(id+"F0.wireOp",EDGE,"E0")}),1.0]])]});
            var Q1;
            {var subQ2=sQuery(id+"F0.wireOp",EDGE,"E68");Q1=makeQuery(id+"F0.imprint","IMPRINT",FACE,{"disambiguationData":[TD([[makeQuery(id+"F0.imprint","IMPRINT",EDGE,{"derivedFrom":subQ2}),1.0]])]});}
            var Q2;
            {var subQ6=sQuery(id+"F0.wireOp",EDGE,"E114");Q2=makeQuery(id+"F0.imprint","IMPRINT",FACE,{"disambiguationData":[TD([[makeQuery(id+"F0.imprint","IMPRINT",EDGE,{"derivedFrom":subQ6}),1.0]])]});}
            var Q3;
            {var subQ4=sQuery(id+"F0.wireOp",EDGE,"E160");Q3=makeQuery(id+"F0.imprint","IMPRINT",FACE,{"disambiguationData":[TD([[makeQuery(id+"F0.imprint","IMPRINT",EDGE,{"derivedFrom":subQ4}),1.0]])]});}
            var Q4;
            {var subQ1=sQuery(id+"F0.wireOp",EDGE,"E229");Q4=makeQuery(id+"F0.imprint","IMPRINT",FACE,{"disambiguationData":[TD([[makeQuery(id+"F0.imprint","IMPRINT",EDGE,{"derivedFrom":subQ1}),1.0]])]});}
            var Q5;
            {var subQ6=sQuery(id+"F0.wireOp",EDGE,"E275");Q5=makeQuery(id+"F0.imprint","IMPRINT",FACE,{"disambiguationData":[TD([[makeQuery(id+"F0.imprint","IMPRINT",EDGE,{"derivedFrom":subQ6}),1.0]])]});}
            extrude(context, id + "F1", {"entities" : qUnion([Q0, Q1, Q2, Q3, Q4, Q5]), "depth" : 10.16 * mm});
        }
        {
            var Q0;
            Q0=makeQuery(id+"F0.imprint","IMPRINT",FACE,{"disambiguationData":[TD([[makeQuery(id+"F0.imprint","IMPRINT",EDGE,{"derivedFrom":sQuery(id+"F0.wireOp",EDGE,"E350")}),1.0]])]});
            var Q1;
            {var subQ0=sQuery(id+"F0.wireOp",EDGE,"E383");Q1=makeQuery(id+"F0.imprint","IMPRINT",FACE,{"disambiguationData":[TD([[makeQuery(id+"F0.imprint","IMPRINT",EDGE,{"derivedFrom":subQ0}),1.0]])]});}
            extrude(context, id + "F2", {"entities" : qUnion([Q0, Q1]), "depth" : 10.16 * mm});
        }
        {
            var Q0;
            {var subQ3=sQuery(id+"F0.wireOp",EDGE,"E380");Q0=makeQuery(id+"F0.imprint","IMPRINT",FACE,{"disambiguationData":[TD([[makeQuery(id+"F0.imprint","IMPRINT",EDGE,{"derivedFrom":subQ3}),1.0]])]});}
            var Q1;
            Q1=makeQuery(id+"F0.imprint","IMPRINT",FACE,{"disambiguationData":[TD([[makeQuery(id+"F0.imprint","IMPRINT",EDGE,{"derivedFrom":sQuery(id+"F0.wireOp",EDGE,"E322")}),1.0]])]});
            var Q2;
            {var subQ2=sQuery(id+"F0.wireOp",EDGE,"E390.0");Q2=makeQuery(id+"F0.imprint","IMPRINT",FACE,{"disambiguationData":[TD([[makeQuery(id+"F0.imprint","IMPRINT",EDGE,{"derivedFrom":subQ2}),-1.0]])]});}
            extrude(context, id + "F3", {"entities" : qUnion([Q0, Q1, Q2]), "depth" : 10.16 * mm});
        }
        {
            var Q0;
            Q0=makeQuery(id+"F0.imprint","IMPRINT",FACE,{"disambiguationData":[TD([[makeQuery(id+"F0.imprint","IMPRINT",EDGE,{"derivedFrom":sQuery(id+"F0.wireOp",EDGE,"E350")}),1.0]])]});
            extrude(context, id + "F4", {"entities" : qUnion([Q0]), "operationType" : NewBodyOperationType.REMOVE, "depth" : 5.08 * mm});
        }
        {
            var Q0;
            Q0=makeQuery(id+"F3.opExtrude","CAP_FACE",FACE,{"disambiguationData":[OSD([sQuery(id+"F0.wireOp",EDGE,"E322"),sQuery(id+"F0.wireOp",EDGE,"E324"),sQuery(id+"F0.wireOp",EDGE,"E325"),sQuery(id+"F0.wireOp",EDGE,"E326"),sQuery(id+"F0.wireOp",EDGE,"E331"),sQuery(id+"F0.wireOp",EDGE,"E332"),sQuery(id+"F0.wireOp",EDGE,"E333"),sQuery(id+"F0.wireOp",EDGE,"E334"),sQuery(id+"F0.wireOp",EDGE,"E335"),sQuery(id+"F0.wireOp",EDGE,"E336"),sQuery(id+"F0.wireOp",EDGE,"E337"),sQuery(id+"F0.wireOp",EDGE,"E338"),sQuery(id+"F0.wireOp",EDGE,"E339"),sQuery(id+"F0.wireOp",EDGE,"E340"),sQuery(id+"F0.wireOp",EDGE,"E341"),sQuery(id+"F0.wireOp",EDGE,"E342"),sQuery(id+"F0.wireOp",EDGE,"E343"),sQuery(id+"F0.wireOp",EDGE,"E344"),sQuery(id+"F0.wireOp",EDGE,"E345"),sQuery(id+"F0.wireOp",EDGE,"E346"),sQuery(id+"F0.wireOp",EDGE,"E347"),sQuery(id+"F0.wireOp",EDGE,"E348"),sQuery(id+"F0.wireOp",EDGE,"E349"),sQuery(id+"F0.wireOp",EDGE,"E379"),sQuery(id+"F0.wireOp",EDGE,"E380"),sQuery(id+"F0.wireOp",EDGE,"E381"),sQuery(id+"F0.wireOp",EDGE,"E382"),sQuery(id+"F0.wireOp",EDGE,"E388"),sQuery(id+"F0.wireOp",EDGE,"E327"),sQuery(id+"F0.wireOp",EDGE,"E328"),sQuery(id+"F0.wireOp",EDGE,"E329"),sQuery(id+"F0.wireOp",EDGE,"E393"),sQuery(id+"F0.wireOp",EDGE,"E392"),sQuery(id+"F0.wireOp",EDGE,"E323"),sQuery(id+"F0.wireOp",EDGE,"E396")])],"isStart":false});
            var sketch = newSketch(context, id + "F5", { "sketchPlane" : qUnion([Q0])});
            skLineSegment(sketch, "E403", {"start": v(11.62, 42.43) * mm, "end": v(11.62, 53.3) * mm});
            skLineSegment(sketch, "E404", {"start": v(21.05, 42.46) * mm, "end": v(21.04, 53.3) * mm});
            skSolve(sketch);
        }
        {
            var Q0;
            {var subQ0=sQuery(id+"F5.wireOp",EDGE,"E403");Q0=makeQuery(id+"F5.imprint","IMPRINT",FACE,{"disambiguationData":[TD([[makeQuery(id+"F5.imprint","IMPRINT",EDGE,{"derivedFrom":subQ0}),-1.0]])]});}
            extrude(context, id + "F6", {"entities" : qUnion([Q0]), "operationType" : NewBodyOperationType.REMOVE, "oppositeDirection" : true, "depth" : 5.08 * mm});
        }
        {
            var Q0;
            {var subQ0=sQuery(id+"F0.wireOp",EDGE,"E347");var subQ1=sQuery(id+"F0.wireOp",EDGE,"E346");var subQ2=sQuery(id+"F0.wireOp",EDGE,"E345");var subQ3=sQuery(id+"F0.wireOp",EDGE,"E344");var subQ4=sQuery(id+"F0.wireOp",EDGE,"E343");var subQ5=sQuery(id+"F0.wireOp",EDGE,"E342");var subQ6=sQuery(id+"F0.wireOp",EDGE,"E341");var subQ7=sQuery(id+"F0.wireOp",EDGE,"E340");var subQ8=sQuery(id+"F0.wireOp",EDGE,"E339");var subQ9=sQuery(id+"F0.wireOp",EDGE,"E338");var subQ10=sQuery(id+"F0.wireOp",EDGE,"E337");var subQ11=sQuery(id+"F0.wireOp",EDGE,"E325");var subQ12=sQuery(id+"F0.wireOp",EDGE,"E324");var subQ13=sQuery(id+"F0.wireOp",EDGE,"E326");var subQ14=sQuery(id+"F0.wireOp",EDGE,"E348");var subQ15=sQuery(id+"F0.wireOp",EDGE,"E322");var subQ16=sQuery(id+"F0.wireOp",EDGE,"E336");var subQ17=sQuery(id+"F0.wireOp",EDGE,"E331");var subQ18=sQuery(id+"F0.wireOp",EDGE,"E332");var subQ19=sQuery(id+"F0.wireOp",EDGE,"E333");var subQ20=sQuery(id+"F0.wireOp",EDGE,"E334");var subQ21=sQuery(id+"F0.wireOp",EDGE,"E335");var subQ22=sQuery(id+"F0.wireOp",EDGE,"E349");var subQ23=sQuery(id+"F0.wireOp",EDGE,"E392");var subQ24=sQuery(id+"F0.wireOp",EDGE,"E382");var subQ25=sQuery(id+"F0.wireOp",EDGE,"E388");var subQ26=sQuery(id+"F0.wireOp",EDGE,"E327");var subQ27=sQuery(id+"F0.wireOp",EDGE,"E328");var subQ28=sQuery(id+"F0.wireOp",EDGE,"E329");var subQ29=sQuery(id+"F0.wireOp",EDGE,"E393");var subQ30=sQuery(id+"F0.wireOp",EDGE,"E323");var subQ31=sQuery(id+"F0.wireOp",EDGE,"E396");Q0=makeQuery(id+"F6.boolean.opBoolean","SPLIT",FACE,{"disambiguationData":[TD([makeQuery(id+"F3.opExtrude","SWEPT_FACE",FACE,{"disambiguationData":[OSD([subQ15])]})])],"derivedFrom":makeQuery(id+"F3.opExtrude","CAP_FACE",FACE,{"disambiguationData":[OSD([subQ15,subQ12,subQ11,subQ13,subQ17,subQ18,subQ19,subQ20,subQ21,subQ16,subQ10,subQ9,subQ8,subQ7,subQ6,subQ5,subQ4,subQ3,subQ2,subQ1,subQ0,subQ14,subQ22,sQuery(id+"F0.wireOp",EDGE,"E379"),sQuery(id+"F0.wireOp",EDGE,"E380"),sQuery(id+"F0.wireOp",EDGE,"E381"),subQ24,subQ25,subQ26,subQ27,subQ28,subQ29,subQ23,subQ30,subQ31])],"isStart":false})});}
            var sketch = newSketch(context, id + "F7", { "sketchPlane" : qUnion([Q0])});
            skLineSegment(sketch, "E405", {"start": v(40.05, 42.54) * mm, "end": v(50.28, 42.58) * mm});
            skSolve(sketch);
        }
        {
            var Q0;
            {var subQ0=sQuery(id+"F7.wireOp",EDGE,"E405");Q0=makeQuery(id+"F7.imprint","IMPRINT",FACE,{"disambiguationData":[TD([[makeQuery(id+"F7.imprint","IMPRINT",EDGE,{"derivedFrom":subQ0}),-1.0]])]});}
            extrude(context, id + "F8", {"entities" : qUnion([Q0]), "operationType" : NewBodyOperationType.REMOVE, "oppositeDirection" : true, "depth" : 5.08 * mm});
        }
        {
            var Q0;
            Q0=makeQuery(id+"F1.opExtrude","SWEPT_BODY",BODY,{"disambiguationData":[OSD([sQuery(id+"F0.wireOp",EDGE,"E0"),sQuery(id+"F0.wireOp",EDGE,"E1"),sQuery(id+"F0.wireOp",EDGE,"E2"),sQuery(id+"F0.wireOp",EDGE,"E3"),sQuery(id+"F0.wireOp",EDGE,"E4"),sQuery(id+"F0.wireOp",EDGE,"E5"),sQuery(id+"F0.wireOp",EDGE,"E6"),sQuery(id+"F0.wireOp",EDGE,"E7"),sQuery(id+"F0.wireOp",EDGE,"E8"),sQuery(id+"F0.wireOp",EDGE,"E9"),sQuery(id+"F0.wireOp",EDGE,"E10"),sQuery(id+"F0.wireOp",EDGE,"E11"),sQuery(id+"F0.wireOp",EDGE,"E12"),sQuery(id+"F0.wireOp",EDGE,"E13"),sQuery(id+"F0.wireOp",EDGE,"E14"),sQuery(id+"F0.wireOp",EDGE,"E15"),sQuery(id+"F0.wireOp",EDGE,"E16"),sQuery(id+"F0.wireOp",EDGE,"E17"),sQuery(id+"F0.wireOp",EDGE,"E18"),sQuery(id+"F0.wireOp",EDGE,"E19"),sQuery(id+"F0.wireOp",EDGE,"E20"),sQuery(id+"F0.wireOp",EDGE,"E21"),sQuery(id+"F0.wireOp",EDGE,"E22"),sQuery(id+"F0.wireOp",EDGE,"E23"),sQuery(id+"F0.wireOp",EDGE,"E24"),sQuery(id+"F0.wireOp",EDGE,"E25"),sQuery(id+"F0.wireOp",EDGE,"E26"),sQuery(id+"F0.wireOp",EDGE,"E27"),sQuery(id+"F0.wireOp",EDGE,"E28"),sQuery(id+"F0.wireOp",EDGE,"E29"),sQuery(id+"F0.wireOp",EDGE,"E30"),sQuery(id+"F0.wireOp",EDGE,"E31"),sQuery(id+"F0.wireOp",EDGE,"E32"),sQuery(id+"F0.wireOp",EDGE,"E33"),sQuery(id+"F0.wireOp",EDGE,"E34"),sQuery(id+"F0.wireOp",EDGE,"E35"),sQuery(id+"F0.wireOp",EDGE,"E36"),sQuery(id+"F0.wireOp",EDGE,"E37"),sQuery(id+"F0.wireOp",EDGE,"E38"),sQuery(id+"F0.wireOp",EDGE,"E39"),sQuery(id+"F0.wireOp",EDGE,"E40"),sQuery(id+"F0.wireOp",EDGE,"E41"),sQuery(id+"F0.wireOp",EDGE,"E42"),sQuery(id+"F0.wireOp",EDGE,"E43"),sQuery(id+"F0.wireOp",EDGE,"E44"),sQuery(id+"F0.wireOp",EDGE,"E45"),sQuery(id+"F0.wireOp",EDGE,"E46"),sQuery(id+"F0.wireOp",EDGE,"E47"),sQuery(id+"F0.wireOp",EDGE,"E48"),sQuery(id+"F0.wireOp",EDGE,"E49"),sQuery(id+"F0.wireOp",EDGE,"E50"),sQuery(id+"F0.wireOp",EDGE,"E51"),sQuery(id+"F0.wireOp",EDGE,"E52"),sQuery(id+"F0.wireOp",EDGE,"E53"),sQuery(id+"F0.wireOp",EDGE,"E54"),sQuery(id+"F0.wireOp",EDGE,"E55"),sQuery(id+"F0.wireOp",EDGE,"E56"),sQuery(id+"F0.wireOp",EDGE,"E57"),sQuery(id+"F0.wireOp",EDGE,"E58"),sQuery(id+"F0.wireOp",EDGE,"E59"),sQuery(id+"F0.wireOp",EDGE,"E60"),sQuery(id+"F0.wireOp",EDGE,"E61"),sQuery(id+"F0.wireOp",EDGE,"E62"),sQuery(id+"F0.wireOp",EDGE,"E63"),sQuery(id+"F0.wireOp",EDGE,"E64"),sQuery(id+"F0.wireOp",EDGE,"E65"),sQuery(id+"F0.wireOp",EDGE,"E66"),sQuery(id+"F0.wireOp",EDGE,"E67"),sQuery(id+"F0.wireOp",EDGE,"E68"),sQuery(id+"F0.wireOp",EDGE,"E69"),sQuery(id+"F0.wireOp",EDGE,"E70"),sQuery(id+"F0.wireOp",EDGE,"E71"),sQuery(id+"F0.wireOp",EDGE,"E72"),sQuery(id+"F0.wireOp",EDGE,"E73"),sQuery(id+"F0.wireOp",EDGE,"E74"),sQuery(id+"F0.wireOp",EDGE,"E75"),sQuery(id+"F0.wireOp",EDGE,"E76"),sQuery(id+"F0.wireOp",EDGE,"E77"),sQuery(id+"F0.wireOp",EDGE,"E78"),sQuery(id+"F0.wireOp",EDGE,"E79"),sQuery(id+"F0.wireOp",EDGE,"E80"),sQuery(id+"F0.wireOp",EDGE,"E81"),sQuery(id+"F0.wireOp",EDGE,"E82"),sQuery(id+"F0.wireOp",EDGE,"E83"),sQuery(id+"F0.wireOp",EDGE,"E84"),sQuery(id+"F0.wireOp",EDGE,"E85"),sQuery(id+"F0.wireOp",EDGE,"E86"),sQuery(id+"F0.wireOp",EDGE,"E87"),sQuery(id+"F0.wireOp",EDGE,"E88"),sQuery(id+"F0.wireOp",EDGE,"E89"),sQuery(id+"F0.wireOp",EDGE,"E90"),sQuery(id+"F0.wireOp",EDGE,"E91"),sQuery(id+"F0.wireOp",EDGE,"E92"),sQuery(id+"F0.wireOp",EDGE,"E93"),sQuery(id+"F0.wireOp",EDGE,"E94"),sQuery(id+"F0.wireOp",EDGE,"E95"),sQuery(id+"F0.wireOp",EDGE,"E96"),sQuery(id+"F0.wireOp",EDGE,"E97"),sQuery(id+"F0.wireOp",EDGE,"E98"),sQuery(id+"F0.wireOp",EDGE,"E99"),sQuery(id+"F0.wireOp",EDGE,"E100"),sQuery(id+"F0.wireOp",EDGE,"E101"),sQuery(id+"F0.wireOp",EDGE,"E102"),sQuery(id+"F0.wireOp",EDGE,"E103"),sQuery(id+"F0.wireOp",EDGE,"E104"),sQuery(id+"F0.wireOp",EDGE,"E105"),sQuery(id+"F0.wireOp",EDGE,"E106"),sQuery(id+"F0.wireOp",EDGE,"E107"),sQuery(id+"F0.wireOp",EDGE,"E108"),sQuery(id+"F0.wireOp",EDGE,"E109"),sQuery(id+"F0.wireOp",EDGE,"E110"),sQuery(id+"F0.wireOp",EDGE,"E111"),sQuery(id+"F0.wireOp",EDGE,"E112"),sQuery(id+"F0.wireOp",EDGE,"E113"),sQuery(id+"F0.wireOp",EDGE,"E114"),sQuery(id+"F0.wireOp",EDGE,"E115"),sQuery(id+"F0.wireOp",EDGE,"E116"),sQuery(id+"F0.wireOp",EDGE,"E117"),sQuery(id+"F0.wireOp",EDGE,"E118"),sQuery(id+"F0.wireOp",EDGE,"E119"),sQuery(id+"F0.wireOp",EDGE,"E120"),sQuery(id+"F0.wireOp",EDGE,"E121"),sQuery(id+"F0.wireOp",EDGE,"E122"),sQuery(id+"F0.wireOp",EDGE,"E123"),sQuery(id+"F0.wireOp",EDGE,"E124"),sQuery(id+"F0.wireOp",EDGE,"E125"),sQuery(id+"F0.wireOp",EDGE,"E126"),sQuery(id+"F0.wireOp",EDGE,"E127"),sQuery(id+"F0.wireOp",EDGE,"E128"),sQuery(id+"F0.wireOp",EDGE,"E129"),sQuery(id+"F0.wireOp",EDGE,"E130"),sQuery(id+"F0.wireOp",EDGE,"E131"),sQuery(id+"F0.wireOp",EDGE,"E132"),sQuery(id+"F0.wireOp",EDGE,"E133"),sQuery(id+"F0.wireOp",EDGE,"E134"),sQuery(id+"F0.wireOp",EDGE,"E135"),sQuery(id+"F0.wireOp",EDGE,"E136"),sQuery(id+"F0.wireOp",EDGE,"E137"),sQuery(id+"F0.wireOp",EDGE,"E138"),sQuery(id+"F0.wireOp",EDGE,"E139"),sQuery(id+"F0.wireOp",EDGE,"E140"),sQuery(id+"F0.wireOp",EDGE,"E141"),sQuery(id+"F0.wireOp",EDGE,"E142"),sQuery(id+"F0.wireOp",EDGE,"E143"),sQuery(id+"F0.wireOp",EDGE,"E144"),sQuery(id+"F0.wireOp",EDGE,"E145"),sQuery(id+"F0.wireOp",EDGE,"E146"),sQuery(id+"F0.wireOp",EDGE,"E147"),sQuery(id+"F0.wireOp",EDGE,"E148"),sQuery(id+"F0.wireOp",EDGE,"E149"),sQuery(id+"F0.wireOp",EDGE,"E150"),sQuery(id+"F0.wireOp",EDGE,"E151"),sQuery(id+"F0.wireOp",EDGE,"E152"),sQuery(id+"F0.wireOp",EDGE,"E153"),sQuery(id+"F0.wireOp",EDGE,"E154"),sQuery(id+"F0.wireOp",EDGE,"E155"),sQuery(id+"F0.wireOp",EDGE,"E156"),sQuery(id+"F0.wireOp",EDGE,"E157"),sQuery(id+"F0.wireOp",EDGE,"E158"),sQuery(id+"F0.wireOp",EDGE,"E159"),sQuery(id+"F0.wireOp",EDGE,"E160"),sQuery(id+"F0.wireOp",EDGE,"E161"),sQuery(id+"F0.wireOp",EDGE,"E162"),sQuery(id+"F0.wireOp",EDGE,"E163"),sQuery(id+"F0.wireOp",EDGE,"E164"),sQuery(id+"F0.wireOp",EDGE,"E165"),sQuery(id+"F0.wireOp",EDGE,"E166"),sQuery(id+"F0.wireOp",EDGE,"E167"),sQuery(id+"F0.wireOp",EDGE,"E168"),sQuery(id+"F0.wireOp",EDGE,"E169"),sQuery(id+"F0.wireOp",EDGE,"E170"),sQuery(id+"F0.wireOp",EDGE,"E171"),sQuery(id+"F0.wireOp",EDGE,"E172"),sQuery(id+"F0.wireOp",EDGE,"E173"),sQuery(id+"F0.wireOp",EDGE,"E174"),sQuery(id+"F0.wireOp",EDGE,"E175"),sQuery(id+"F0.wireOp",EDGE,"E176"),sQuery(id+"F0.wireOp",EDGE,"E177"),sQuery(id+"F0.wireOp",EDGE,"E178"),sQuery(id+"F0.wireOp",EDGE,"E179"),sQuery(id+"F0.wireOp",EDGE,"E180"),sQuery(id+"F0.wireOp",EDGE,"E181"),sQuery(id+"F0.wireOp",EDGE,"E182"),sQuery(id+"F0.wireOp",EDGE,"E183"),sQuery(id+"F0.wireOp",EDGE,"E184"),sQuery(id+"F0.wireOp",EDGE,"E185"),sQuery(id+"F0.wireOp",EDGE,"E186"),sQuery(id+"F0.wireOp",EDGE,"E187"),sQuery(id+"F0.wireOp",EDGE,"E188"),sQuery(id+"F0.wireOp",EDGE,"E189"),sQuery(id+"F0.wireOp",EDGE,"E190"),sQuery(id+"F0.wireOp",EDGE,"E191"),sQuery(id+"F0.wireOp",EDGE,"E192"),sQuery(id+"F0.wireOp",EDGE,"E193"),sQuery(id+"F0.wireOp",EDGE,"E194"),sQuery(id+"F0.wireOp",EDGE,"E195"),sQuery(id+"F0.wireOp",EDGE,"E196"),sQuery(id+"F0.wireOp",EDGE,"E197"),sQuery(id+"F0.wireOp",EDGE,"E198"),sQuery(id+"F0.wireOp",EDGE,"E199"),sQuery(id+"F0.wireOp",EDGE,"E200"),sQuery(id+"F0.wireOp",EDGE,"E201"),sQuery(id+"F0.wireOp",EDGE,"E202"),sQuery(id+"F0.wireOp",EDGE,"E203"),sQuery(id+"F0.wireOp",EDGE,"E204"),sQuery(id+"F0.wireOp",EDGE,"E205"),sQuery(id+"F0.wireOp",EDGE,"E206"),sQuery(id+"F0.wireOp",EDGE,"E207"),sQuery(id+"F0.wireOp",EDGE,"E208"),sQuery(id+"F0.wireOp",EDGE,"E209"),sQuery(id+"F0.wireOp",EDGE,"E210"),sQuery(id+"F0.wireOp",EDGE,"E211"),sQuery(id+"F0.wireOp",EDGE,"E212"),sQuery(id+"F0.wireOp",EDGE,"E213"),sQuery(id+"F0.wireOp",EDGE,"E214"),sQuery(id+"F0.wireOp",EDGE,"E215"),sQuery(id+"F0.wireOp",EDGE,"E216"),sQuery(id+"F0.wireOp",EDGE,"E217"),sQuery(id+"F0.wireOp",EDGE,"E218"),sQuery(id+"F0.wireOp",EDGE,"E219"),sQuery(id+"F0.wireOp",EDGE,"E220"),sQuery(id+"F0.wireOp",EDGE,"E221"),sQuery(id+"F0.wireOp",EDGE,"E222"),sQuery(id+"F0.wireOp",EDGE,"E223"),sQuery(id+"F0.wireOp",EDGE,"E224"),sQuery(id+"F0.wireOp",EDGE,"E225"),sQuery(id+"F0.wireOp",EDGE,"E226"),sQuery(id+"F0.wireOp",EDGE,"E227"),sQuery(id+"F0.wireOp",EDGE,"E228"),sQuery(id+"F0.wireOp",EDGE,"E229"),sQuery(id+"F0.wireOp",EDGE,"E230"),sQuery(id+"F0.wireOp",EDGE,"E231"),sQuery(id+"F0.wireOp",EDGE,"E232"),sQuery(id+"F0.wireOp",EDGE,"E233"),sQuery(id+"F0.wireOp",EDGE,"E234"),sQuery(id+"F0.wireOp",EDGE,"E235"),sQuery(id+"F0.wireOp",EDGE,"E236"),sQuery(id+"F0.wireOp",EDGE,"E237"),sQuery(id+"F0.wireOp",EDGE,"E238"),sQuery(id+"F0.wireOp",EDGE,"E239"),sQuery(id+"F0.wireOp",EDGE,"E240"),sQuery(id+"F0.wireOp",EDGE,"E241"),sQuery(id+"F0.wireOp",EDGE,"E242"),sQuery(id+"F0.wireOp",EDGE,"E243"),sQuery(id+"F0.wireOp",EDGE,"E244"),sQuery(id+"F0.wireOp",EDGE,"E245"),sQuery(id+"F0.wireOp",EDGE,"E246"),sQuery(id+"F0.wireOp",EDGE,"E247"),sQuery(id+"F0.wireOp",EDGE,"E248"),sQuery(id+"F0.wireOp",EDGE,"E249"),sQuery(id+"F0.wireOp",EDGE,"E250"),sQuery(id+"F0.wireOp",EDGE,"E251"),sQuery(id+"F0.wireOp",EDGE,"E252"),sQuery(id+"F0.wireOp",EDGE,"E253"),sQuery(id+"F0.wireOp",EDGE,"E254"),sQuery(id+"F0.wireOp",EDGE,"E255"),sQuery(id+"F0.wireOp",EDGE,"E256"),sQuery(id+"F0.wireOp",EDGE,"E257"),sQuery(id+"F0.wireOp",EDGE,"E258"),sQuery(id+"F0.wireOp",EDGE,"E259"),sQuery(id+"F0.wireOp",EDGE,"E260"),sQuery(id+"F0.wireOp",EDGE,"E261"),sQuery(id+"F0.wireOp",EDGE,"E262"),sQuery(id+"F0.wireOp",EDGE,"E263"),sQuery(id+"F0.wireOp",EDGE,"E264"),sQuery(id+"F0.wireOp",EDGE,"E265"),sQuery(id+"F0.wireOp",EDGE,"E266"),sQuery(id+"F0.wireOp",EDGE,"E267"),sQuery(id+"F0.wireOp",EDGE,"E268"),sQuery(id+"F0.wireOp",EDGE,"E269"),sQuery(id+"F0.wireOp",EDGE,"E270"),sQuery(id+"F0.wireOp",EDGE,"E271"),sQuery(id+"F0.wireOp",EDGE,"E272"),sQuery(id+"F0.wireOp",EDGE,"E273"),sQuery(id+"F0.wireOp",EDGE,"E274"),sQuery(id+"F0.wireOp",EDGE,"E275"),sQuery(id+"F0.wireOp",EDGE,"E276"),sQuery(id+"F0.wireOp",EDGE,"E277"),sQuery(id+"F0.wireOp",EDGE,"E278"),sQuery(id+"F0.wireOp",EDGE,"E279"),sQuery(id+"F0.wireOp",EDGE,"E280"),sQuery(id+"F0.wireOp",EDGE,"E281"),sQuery(id+"F0.wireOp",EDGE,"E282"),sQuery(id+"F0.wireOp",EDGE,"E283"),sQuery(id+"F0.wireOp",EDGE,"E284"),sQuery(id+"F0.wireOp",EDGE,"E285"),sQuery(id+"F0.wireOp",EDGE,"E286"),sQuery(id+"F0.wireOp",EDGE,"E287"),sQuery(id+"F0.wireOp",EDGE,"E288"),sQuery(id+"F0.wireOp",EDGE,"E289"),sQuery(id+"F0.wireOp",EDGE,"E290"),sQuery(id+"F0.wireOp",EDGE,"E291"),sQuery(id+"F0.wireOp",EDGE,"E292"),sQuery(id+"F0.wireOp",EDGE,"E293"),sQuery(id+"F0.wireOp",EDGE,"E294"),sQuery(id+"F0.wireOp",EDGE,"E295"),sQuery(id+"F0.wireOp",EDGE,"E296"),sQuery(id+"F0.wireOp",EDGE,"E297"),sQuery(id+"F0.wireOp",EDGE,"E298"),sQuery(id+"F0.wireOp",EDGE,"E299"),sQuery(id+"F0.wireOp",EDGE,"E300"),sQuery(id+"F0.wireOp",EDGE,"E301"),sQuery(id+"F0.wireOp",EDGE,"E302"),sQuery(id+"F0.wireOp",EDGE,"E303"),sQuery(id+"F0.wireOp",EDGE,"E304"),sQuery(id+"F0.wireOp",EDGE,"E305"),sQuery(id+"F0.wireOp",EDGE,"E306"),sQuery(id+"F0.wireOp",EDGE,"E307"),sQuery(id+"F0.wireOp",EDGE,"E308"),sQuery(id+"F0.wireOp",EDGE,"E309"),sQuery(id+"F0.wireOp",EDGE,"E310"),sQuery(id+"F0.wireOp",EDGE,"E311"),sQuery(id+"F0.wireOp",EDGE,"E312"),sQuery(id+"F0.wireOp",EDGE,"E313"),sQuery(id+"F0.wireOp",EDGE,"E314"),sQuery(id+"F0.wireOp",EDGE,"E315"),sQuery(id+"F0.wireOp",EDGE,"E316"),sQuery(id+"F0.wireOp",EDGE,"E317"),sQuery(id+"F0.wireOp",EDGE,"E318"),sQuery(id+"F0.wireOp",EDGE,"E319"),sQuery(id+"F0.wireOp",EDGE,"E320"),sQuery(id+"F0.wireOp",EDGE,"E321")])]});
            transform(context, id + "F9", {"entities" : qUnion([Q0]), "transformType" : TransformType.TRANSLATION_3D, "dx" : 97.54 * mm, "dy" : 0 * mm, "dz" : 0 * mm, "makeCopy" : true});
        }
    });
